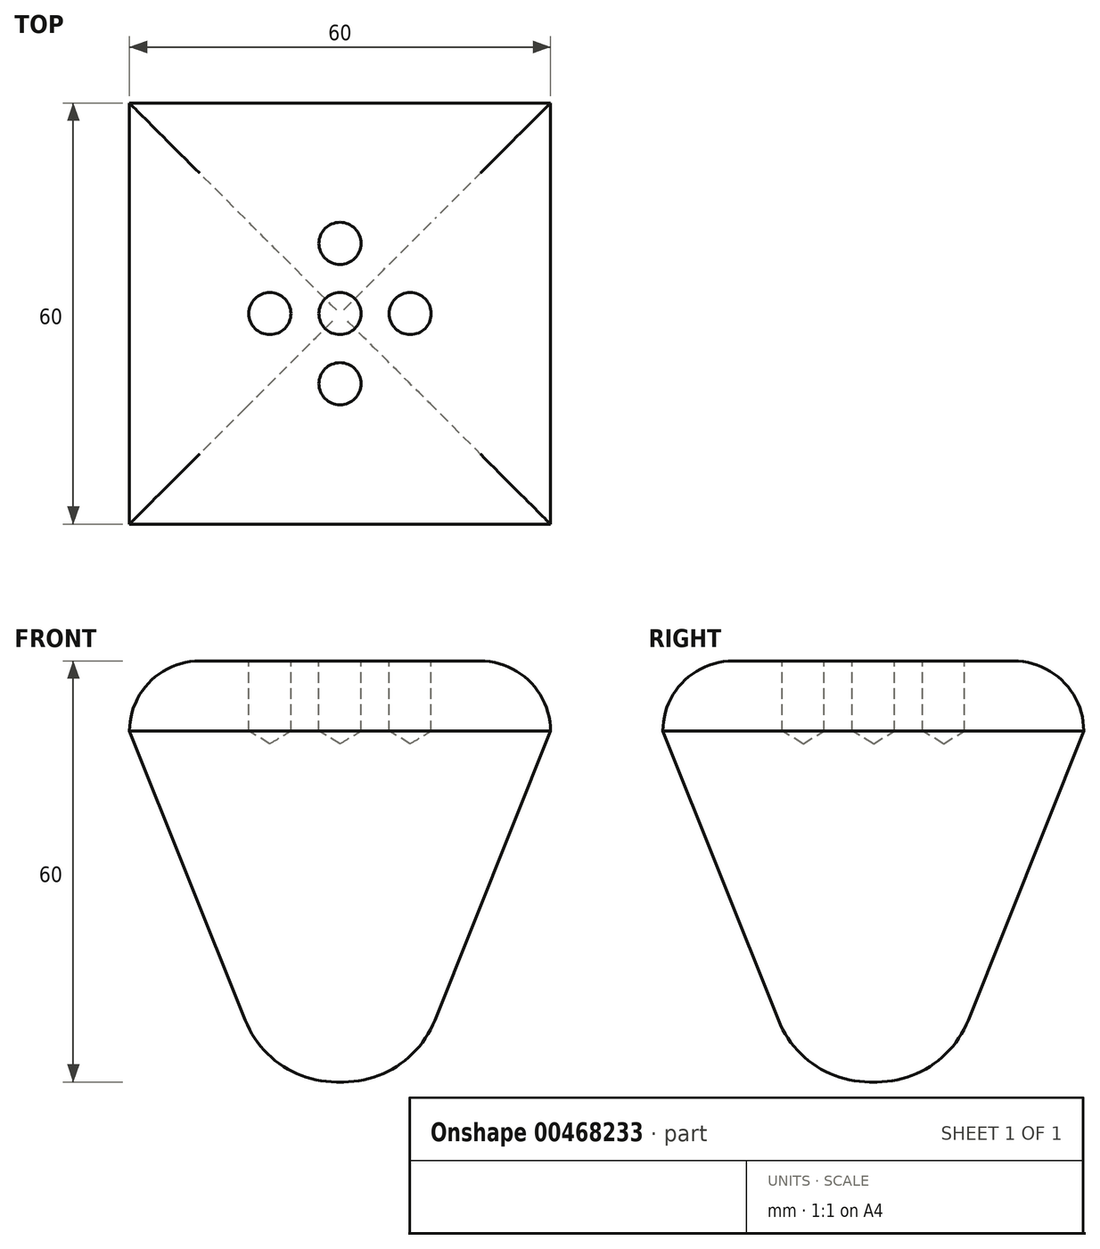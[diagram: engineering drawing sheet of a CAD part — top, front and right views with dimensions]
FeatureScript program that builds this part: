
annotation { "Feature Type Name" : "Feature", "Feature Type Description" : "" }
export const myFeature = defineFeature(function(context is Context, id is Id, definition is map)
    precondition{}
    {
        {
            var Q0;
            Q0=qCreatedBy(makeId("Top.planeOp"),FACE);
            var sketch = newSketch(context, id + "F0", { "sketchPlane" : qUnion([Q0])});
            skLineSegment(sketch, "E0.bottom", {"start": v(30, -30) * mm, "end": v(-30, -30) * mm});
            skLineSegment(sketch, "E0.top", {"start": v(30, 30) * mm, "end": v(-30, 30) * mm});
            skLineSegment(sketch, "E0.left", {"start": v(30, -30) * mm, "end": v(30, 30) * mm});
            skLineSegment(sketch, "E0.right", {"start": v(-30, -30) * mm, "end": v(-30, 30) * mm});
            skPoint(sketch, "E0.middle", {"position": v(0, 0) * mm});
            skSolve(sketch);
        }
        {
            var Q0;
            Q0=makeQuery(id+"F0.imprint","IMPRINT",FACE,{"disambiguationData":[TD([[makeQuery(id+"F0.imprint","IMPRINT",EDGE,{"derivedFrom":sQuery(id+"F0.wireOp",EDGE,"E0.bottom")}),-1.0]])]});
            extrude(context, id + "F1", {"entities" : qUnion([Q0]), "depth" : 60 * mm});
        }
        {
            var Q0;
            Q0=makeQuery(id+"F1.opExtrude","CAP_FACE",FACE,{"disambiguationData":[OSD([sQuery(id+"F0.wireOp",EDGE,"E0.bottom"),sQuery(id+"F0.wireOp",EDGE,"E0.top"),sQuery(id+"F0.wireOp",EDGE,"E0.left"),sQuery(id+"F0.wireOp",EDGE,"E0.right")])],"isStart":false});
            var sketch = newSketch(context, id + "F2", { "sketchPlane" : qUnion([Q0])});
            skLineSegment(sketch, "E1", {"start": v(0, 0) * mm, "end": v(0, 10) * mm});
            skLineSegment(sketch, "E2", {"start": v(0, 0) * mm, "end": v(0, -10) * mm});
            skLineSegment(sketch, "E3", {"start": v(0, 0) * mm, "end": v(-10, 0) * mm});
            skLineSegment(sketch, "E4", {"start": v(0, 0) * mm, "end": v(10, 0) * mm});
            skSolve(sketch);
        }
        {
            var Q0;
            Q0=sQuery(id+"F2.wireOp",VERTEX,"E1.end");
            var Q1;
            Q1=sQuery(id+"F2.wireOp",VERTEX,"E3.end");
            var Q2;
            Q2=sQuery(id+"F2.wireOp",VERTEX,"E4.end");
            var Q3;
            Q3=sQuery(id+"F2.wireOp",VERTEX,"E2.end");
            var Q4;
            Q4=sQuery(id+"F2.wireOp",VERTEX,"E4.start");
            var Q5;
            Q5=makeQuery(id+"F1.opExtrude","SWEPT_BODY",BODY,{"disambiguationData":[OSD([sQuery(id+"F0.wireOp",EDGE,"E0.bottom"),sQuery(id+"F0.wireOp",EDGE,"E0.top"),sQuery(id+"F0.wireOp",EDGE,"E0.left"),sQuery(id+"F0.wireOp",EDGE,"E0.right")])]});
            hole(context, id + "F3", {"style" : HoleStyle.SIMPLE, "endStyle" : HoleEndStyle.BLIND, "holeDiameter" : 6 * mm, "holeDepth" : 10 * mm, "isTappedThrough" : true, "tappedDepth" : 12 * mm, "tapClearance" : 3, "locations" : qUnion([Q0, Q1, Q2, Q3, Q4]), "scope" : qUnion([Q5])});
        }
        {
            var Q0;
            Q0=makeQuery(id+"F1.opExtrude","CAP_EDGE",EDGE,{"disambiguationData":[OSD([sQuery(id+"F0.wireOp",EDGE,"E0.right")])],"isStart":true});
            var Q1;
            Q1=makeQuery(id+"F1.opExtrude","CAP_FACE",FACE,{"disambiguationData":[OSD([sQuery(id+"F0.wireOp",EDGE,"E0.bottom"),sQuery(id+"F0.wireOp",EDGE,"E0.top"),sQuery(id+"F0.wireOp",EDGE,"E0.left"),sQuery(id+"F0.wireOp",EDGE,"E0.right")])],"isStart":true});
            chamfer(context, id + "F4", {"entities" : qUnion([Q0, Q1]), "chamferType" : ChamferType.TWO_OFFSETS, "width1" : 20 * mm, "oppositeDirection" : false, "width2" : 50 * mm, "tangentPropagation" : true});
        }
        {
            var Q0;
            Q0=makeQuery(id+"F1.opExtrude","CAP_FACE",FACE,{"disambiguationData":[OSD([sQuery(id+"F0.wireOp",EDGE,"E0.bottom"),sQuery(id+"F0.wireOp",EDGE,"E0.top"),sQuery(id+"F0.wireOp",EDGE,"E0.left"),sQuery(id+"F0.wireOp",EDGE,"E0.right")])],"isStart":true});
            fillet(context, id + "F5", {"entities" : qUnion([Q0]), "radius" : 14 * mm, "tangentPropagation" : true, "allowEdgeOverflow" : false});
        }
        {
            var Q0;
            Q0=makeQuery(id+"F1.opExtrude","CAP_EDGE",EDGE,{"disambiguationData":[OSD([sQuery(id+"F0.wireOp",EDGE,"E0.right")])],"isStart":false});
            var Q1;
            Q1=makeQuery(id+"F1.opExtrude","CAP_EDGE",EDGE,{"disambiguationData":[OSD([sQuery(id+"F0.wireOp",EDGE,"E0.top")])],"isStart":false});
            var Q2;
            Q2=makeQuery(id+"F1.opExtrude","CAP_EDGE",EDGE,{"disambiguationData":[OSD([sQuery(id+"F0.wireOp",EDGE,"E0.left")])],"isStart":false});
            var Q3;
            Q3=makeQuery(id+"F1.opExtrude","CAP_EDGE",EDGE,{"disambiguationData":[OSD([sQuery(id+"F0.wireOp",EDGE,"E0.bottom")])],"isStart":false});
            fillet(context, id + "F6", {"entities" : qUnion([Q0, Q1, Q2, Q3]), "radius" : 10 * mm, "tangentPropagation" : true, "allowEdgeOverflow" : false});
        }
    });
